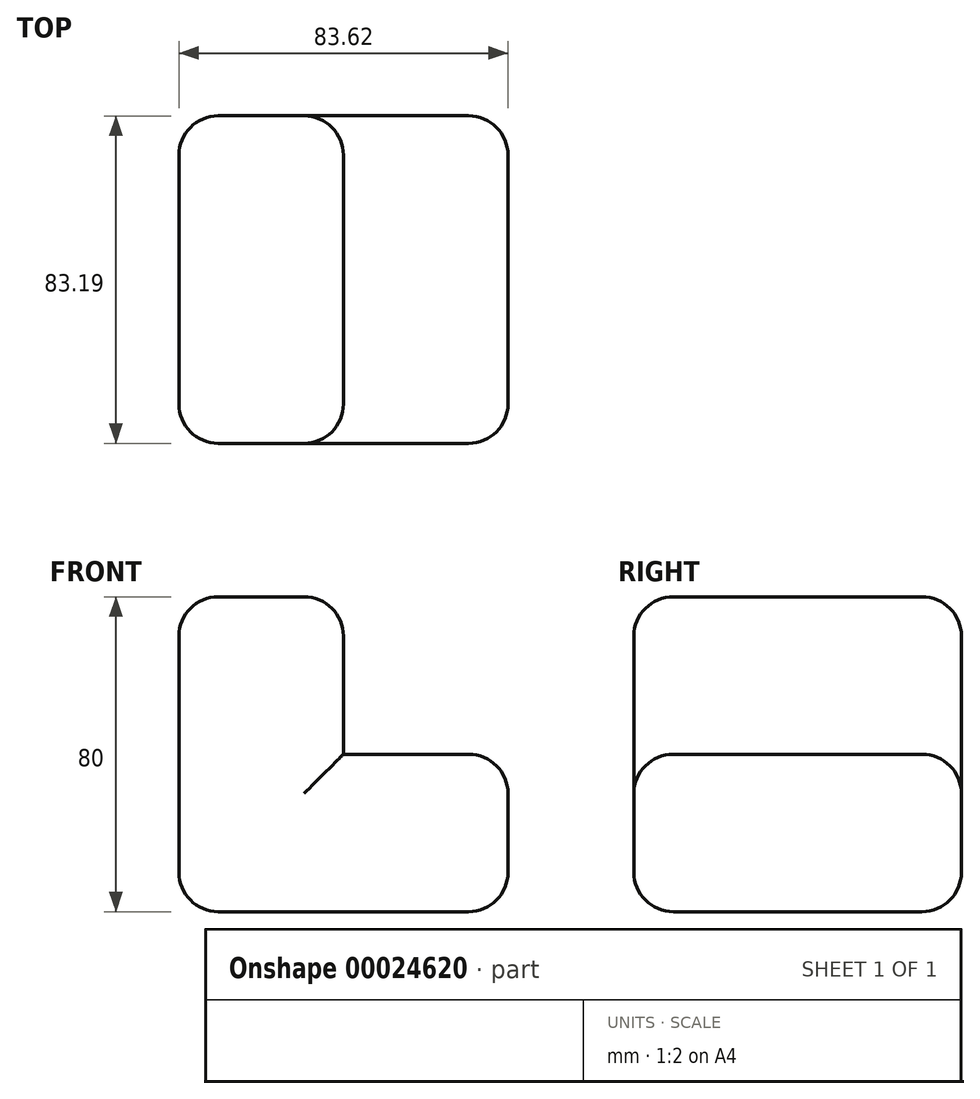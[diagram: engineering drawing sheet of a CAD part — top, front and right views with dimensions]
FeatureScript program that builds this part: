
annotation { "Feature Type Name" : "Feature", "Feature Type Description" : "" }
export const myFeature = defineFeature(function(context is Context, id is Id, definition is map)
    precondition{}
    {
        {
            var Q0;
            Q0=qCreatedBy(makeId("Top.planeOp"),FACE);
            var sketch = newSketch(context, id + "F0", { "sketchPlane" : qUnion([Q0])});
            skLineSegment(sketch, "E0.bottom", {"start": v(-59.13, -45.93) * mm, "end": v(24.5, -45.93) * mm});
            skLineSegment(sketch, "E0.top", {"start": v(-59.13, 37.26) * mm, "end": v(24.5, 37.26) * mm});
            skLineSegment(sketch, "E0.left", {"start": v(-59.13, -45.93) * mm, "end": v(-59.13, 37.26) * mm});
            skLineSegment(sketch, "E0.right", {"start": v(24.5, -45.93) * mm, "end": v(24.5, 37.26) * mm});
            skSolve(sketch);
        }
        {
            var Q0;
            Q0=makeQuery(id+"F0.imprint","IMPRINT",FACE,{"disambiguationData":[TD([[makeQuery(id+"F0.imprint","IMPRINT",EDGE,{"derivedFrom":sQuery(id+"F0.wireOp",EDGE,"E0.bottom")}),1.0]])]});
            extrude(context, id + "F1", {"entities" : qUnion([Q0]), "depth" : 40 * mm});
        }
        {
            var Q0;
            Q0=makeQuery(id+"F1.opExtrude","CAP_FACE",FACE,{"disambiguationData":[OSD([sQuery(id+"F0.wireOp",EDGE,"E0.bottom"),sQuery(id+"F0.wireOp",EDGE,"E0.top"),sQuery(id+"F0.wireOp",EDGE,"E0.left"),sQuery(id+"F0.wireOp",EDGE,"E0.right")])],"isStart":false});
            var sketch = newSketch(context, id + "F2", { "sketchPlane" : qUnion([Q0])});
            skLineSegment(sketch, "E1", {"start": v(-17.32, 37.26) * mm, "end": v(-17.32, -45.93) * mm});
            skSolve(sketch);
        }
        {
            var Q0;
            {var subQ1=sQuery(id+"F2.wireOp",EDGE,"E1");Q0=makeQuery(id+"F2.imprint","IMPRINT",FACE,{"disambiguationData":[TD([[makeQuery(id+"F2.imprint","IMPRINT",EDGE,{"derivedFrom":subQ1}),-1.0]])]});}
            extrude(context, id + "F3", {"entities" : qUnion([Q0]), "operationType" : NewBodyOperationType.ADD, "depth" : 40 * mm});
        }
        {
            var Q0;
            Q0=makeQuery(id+"F3.opExtrude","CAP_EDGE",EDGE,{"disambiguationData":[OSD([sQuery(id+"F0.wireOp",EDGE,"E0.bottom")])],"isStart":false});
            var Q1;
            Q1=makeQuery(id+"F3.opExtrude","CAP_EDGE",EDGE,{"disambiguationData":[OSD([sQuery(id+"F2.wireOp",EDGE,"E1")])],"isStart":false});
            var Q2;
            Q2=makeQuery(id+"F3.opExtrude","SWEPT_EDGE",EDGE,{"disambiguationData":[OSD([sQuery(id+"F0.wireOp",EDGE,"E0.bottom"),sQuery(id+"F2.wireOp",EDGE,"E1")])]});
            var Q3;
            Q3=makeQuery(id+"F3.opExtrude","CAP_EDGE",EDGE,{"disambiguationData":[OSD([sQuery(id+"F2.wireOp",EDGE,"E1")])],"isStart":true});
            var Q4;
            Q4=makeQuery(id+"F1.opExtrude","CAP_EDGE",EDGE,{"disambiguationData":[OSD([sQuery(id+"F0.wireOp",EDGE,"E0.bottom")])],"isStart":false});
            var Q5;
            Q5=makeQuery(id+"F1.opExtrude","SWEPT_EDGE",EDGE,{"disambiguationData":[OSD([sQuery(id+"F0.wireOp",EDGE,"E0.bottom"),sQuery(id+"F0.wireOp",EDGE,"E0.right")])]});
            var Q6;
            Q6=makeQuery(id+"F1.opExtrude","CAP_EDGE",EDGE,{"disambiguationData":[OSD([sQuery(id+"F0.wireOp",EDGE,"E0.right")])],"isStart":false});
            var Q7;
            Q7=makeQuery(id+"F1.opExtrude","SWEPT_EDGE",EDGE,{"disambiguationData":[OSD([sQuery(id+"F0.wireOp",EDGE,"E0.top"),sQuery(id+"F0.wireOp",EDGE,"E0.right")])]});
            var Q8;
            Q8=makeQuery(id+"F1.opExtrude","CAP_EDGE",EDGE,{"disambiguationData":[OSD([sQuery(id+"F0.wireOp",EDGE,"E0.right")])],"isStart":true});
            var Q9;
            Q9=makeQuery(id+"F1.opExtrude","CAP_EDGE",EDGE,{"disambiguationData":[OSD([sQuery(id+"F0.wireOp",EDGE,"E0.bottom")])],"isStart":true});
            var Q10;
            {var subQ0=sQuery(id+"F0.wireOp",EDGE,"E0.bottom");var subQ1=sQuery(id+"F0.wireOp",EDGE,"E0.left");Q10=makeQuery(id+"F3.boolean.opBoolean","MERGE",EDGE,{"derivedFrom":[makeQuery(id+"F1.opExtrude","SWEPT_EDGE",EDGE,{"disambiguationData":[OSD([subQ0,subQ1])]}),makeQuery(id+"F3.opExtrude","SWEPT_EDGE",EDGE,{"disambiguationData":[OSD([subQ0,subQ1])]})]});}
            var Q11;
            Q11=makeQuery(id+"F3.opExtrude","CAP_EDGE",EDGE,{"disambiguationData":[OSD([sQuery(id+"F0.wireOp",EDGE,"E0.top")])],"isStart":false});
            var Q12;
            Q12=makeQuery(id+"F3.opExtrude","CAP_EDGE",EDGE,{"disambiguationData":[OSD([sQuery(id+"F0.wireOp",EDGE,"E0.left")])],"isStart":false});
            var Q13;
            {var subQ0=sQuery(id+"F0.wireOp",EDGE,"E0.top");var subQ1=sQuery(id+"F0.wireOp",EDGE,"E0.left");Q13=makeQuery(id+"F3.boolean.opBoolean","MERGE",EDGE,{"derivedFrom":[makeQuery(id+"F1.opExtrude","SWEPT_EDGE",EDGE,{"disambiguationData":[OSD([subQ0,subQ1])]}),makeQuery(id+"F3.opExtrude","SWEPT_EDGE",EDGE,{"disambiguationData":[OSD([subQ0,subQ1])]})]});}
            var Q14;
            Q14=makeQuery(id+"F1.opExtrude","CAP_EDGE",EDGE,{"disambiguationData":[OSD([sQuery(id+"F0.wireOp",EDGE,"E0.left")])],"isStart":true});
            var Q15;
            Q15=makeQuery(id+"F1.opExtrude","CAP_EDGE",EDGE,{"disambiguationData":[OSD([sQuery(id+"F0.wireOp",EDGE,"E0.top")])],"isStart":false});
            var Q16;
            Q16=makeQuery(id+"F3.opExtrude","SWEPT_EDGE",EDGE,{"disambiguationData":[OSD([sQuery(id+"F0.wireOp",EDGE,"E0.top"),sQuery(id+"F2.wireOp",EDGE,"E1")])]});
            var Q17;
            Q17=makeQuery(id+"F1.opExtrude","CAP_EDGE",EDGE,{"disambiguationData":[OSD([sQuery(id+"F0.wireOp",EDGE,"E0.top")])],"isStart":true});
            fillet(context, id + "F4", {"entities" : qUnion([Q0, Q1, Q2, Q3, Q4, Q5, Q6, Q7, Q8, Q9, Q10, Q11, Q12, Q13, Q14, Q15, Q16, Q17]), "radius" : 10 * mm, "tangentPropagation" : true, "allowEdgeOverflow" : false});
        }
    });
